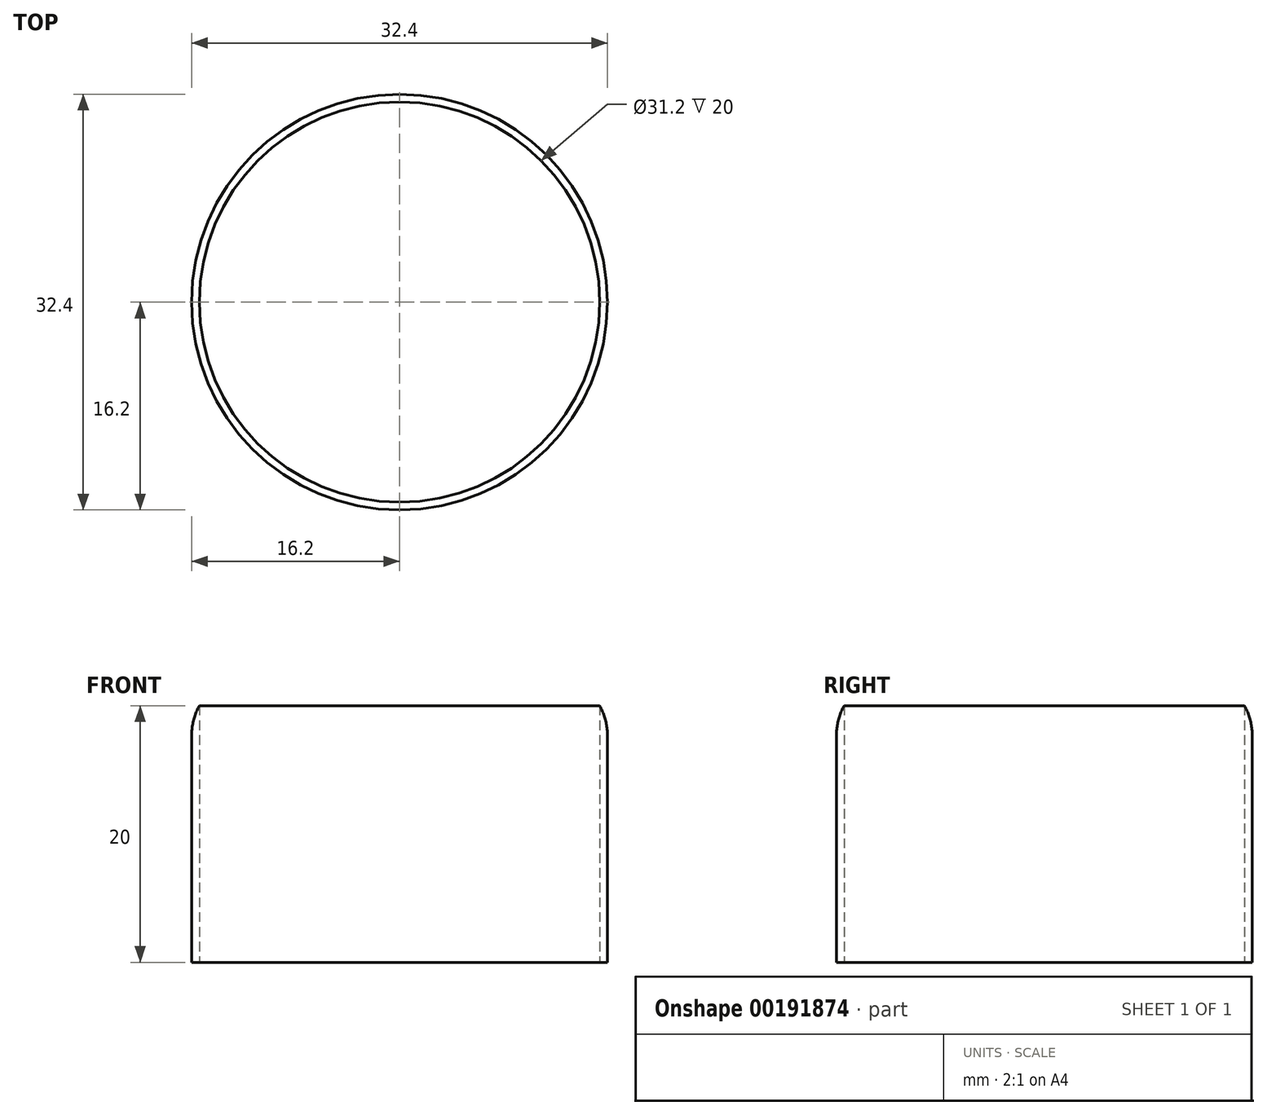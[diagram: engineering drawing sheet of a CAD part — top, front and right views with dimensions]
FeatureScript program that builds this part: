
annotation { "Feature Type Name" : "Feature", "Feature Type Description" : "" }
export const myFeature = defineFeature(function(context is Context, id is Id, definition is map)
    precondition{}
    {
        {
            var Q0;
            Q0=qCreatedBy(makeId("Top.planeOp"),FACE);
            var sketch = newSketch(context, id + "F0", { "sketchPlane" : qUnion([Q0])});
            skCircle(sketch, "E0", {"center": v(0, 0) * mm, "radius": 15.6 * mm});
            skCircle(sketch, "E1.0", {"center": v(0, 0) * mm, "radius": 16.2 * mm});
            skSolve(sketch);
        }
        {
            var Q0;
            Q0=makeQuery(id+"F0.imprint","IMPRINT",FACE,{"disambiguationData":[TD([[makeQuery(id+"F0.imprint","IMPRINT",EDGE,{"derivedFrom":sQuery(id+"F0.wireOp",EDGE,"E0")}),-1.0]])]});
            var Q1;
            Q1=sQuery(id+"F0.wireOp",EDGE,"E0");
            var Q2;
            Q2=sQuery(id+"F0.wireOp",EDGE,"d55485ba-e18b-4eff-a78f-b738d040bdc0.0");
            extrude(context, id + "F1", {"entities" : qUnion([Q0]), "surfaceEntities" : qUnion([Q1, Q2]), "depth" : 20 * mm});
        }
        {
            var Q0;
            Q0=makeQuery(id+"F1.opExtrude","CAP_EDGE",EDGE,{"disambiguationData":[OSD([sQuery(id+"F0.wireOp",EDGE,"d55485ba-e18b-4eff-a78f-b738d040bdc0.0")])],"isStart":false});
            var Q1;
            Q1=makeQuery(id+"F1.opExtrude","CAP_EDGE",EDGE,{"disambiguationData":[OSD([sQuery(id+"F0.wireOp",EDGE,"E1.0")])],"isStart":false});
            fillet(context, id + "F2", {"entities" : qUnion([Q0, Q1]), "radius" : 5 * mm, "tangentPropagation" : true, "allowEdgeOverflow" : false});
        }
    });
